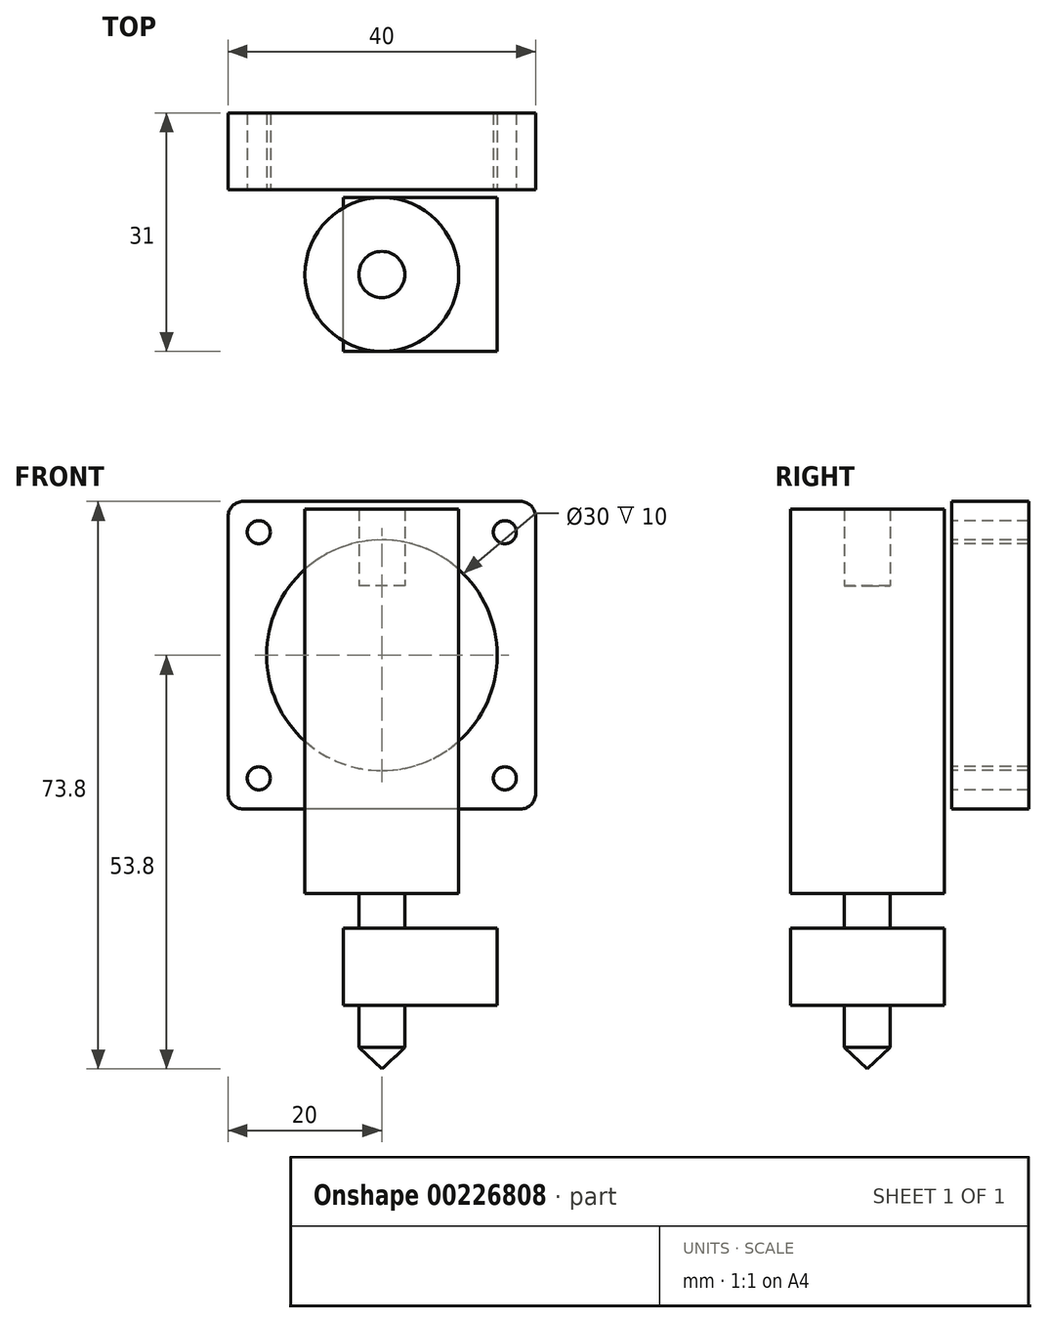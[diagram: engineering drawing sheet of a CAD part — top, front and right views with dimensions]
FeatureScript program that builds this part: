
annotation { "Feature Type Name" : "Feature", "Feature Type Description" : "" }
export const myFeature = defineFeature(function(context is Context, id is Id, definition is map)
    precondition{}
    {
        {
            var Q0;
            Q0=qCreatedBy(makeId("Top.planeOp"),FACE);
            var sketch = newSketch(context, id + "F0", { "sketchPlane" : qUnion([Q0])});
            skCircle(sketch, "E0", {"center": v(0, 0) * mm, "radius": 8 * mm});
            skCircle(sketch, "E1", {"center": v(0, 0) * mm, "radius": 10 * mm});
            skCircle(sketch, "E2", {"center": v(0, 0) * mm, "radius": 3 * mm});
            skSolve(sketch);
        }
        {
            var Q0;
            Q0=makeQuery(id+"F0.imprint","IMPRINT",FACE,{"disambiguationData":[TD([[makeQuery(id+"F0.imprint","IMPRINT",EDGE,{"derivedFrom":sQuery(id+"F0.wireOp",EDGE,"E0")}),1.0]])]});
            var Q1;
            Q1=makeQuery(id+"F0.imprint","IMPRINT",FACE,{"disambiguationData":[TD([[makeQuery(id+"F0.imprint","IMPRINT",EDGE,{"derivedFrom":sQuery(id+"F0.wireOp",EDGE,"E0")}),-1.0]])]});
            extrude(context, id + "F1", {"entities" : qUnion([Q0, Q1]), "depth" : 10 * mm});
        }
        {
            var Q0;
            Q0=makeQuery(id+"F0.imprint","IMPRINT",FACE,{"disambiguationData":[TD([[makeQuery(id+"F0.imprint","IMPRINT",EDGE,{"derivedFrom":sQuery(id+"F0.wireOp",EDGE,"E0")}),-1.0]])]});
            var Q1;
            Q1=makeQuery(id+"F0.imprint","IMPRINT",FACE,{"disambiguationData":[TD([[makeQuery(id+"F0.imprint","IMPRINT",EDGE,{"derivedFrom":sQuery(id+"F0.wireOp",EDGE,"E0")}),1.0]])]});
            var Q2;
            Q2=makeQuery(id+"F0.imprint","IMPRINT",FACE,{"disambiguationData":[TD([[makeQuery(id+"F0.imprint","IMPRINT",EDGE,{"derivedFrom":sQuery(id+"F0.wireOp",EDGE,"E2")}),1.0]])]});
            extrude(context, id + "F2", {"entities" : qUnion([Q0, Q1, Q2]), "operationType" : NewBodyOperationType.ADD, "oppositeDirection" : true, "depth" : 40 * mm});
        }
        {
            var Q0;
            Q0=makeQuery(id+"F0.imprint","IMPRINT",FACE,{"disambiguationData":[TD([[makeQuery(id+"F0.imprint","IMPRINT",EDGE,{"derivedFrom":sQuery(id+"F0.wireOp",EDGE,"E2")}),1.0]])]});
            extrude(context, id + "F3", {"entities" : qUnion([Q0]), "operationType" : NewBodyOperationType.ADD, "oppositeDirection" : true, "depth" : 60 * mm});
        }
        {
            var Q0;
            Q0=qCreatedBy(makeId("Front.planeOp"),FACE);
            var sketch = newSketch(context, id + "F4", { "sketchPlane" : qUnion([Q0])});
            skLineSegment(sketch, "E3.0", {"start": v(-3, -44.5) * mm, "end": v(3, -44.5) * mm});
            skLineSegment(sketch, "E4", {"start": v(0, 0) * mm, "end": v(0, -62.8) * mm, "construction": true});
            skPoint(sketch, "E4.endSnap0", {"position": v(0, -44.5) * mm});
            skLineSegment(sketch, "E5.bottom", {"start": v(-5, -44.5) * mm, "end": v(15, -44.5) * mm});
            skLineSegment(sketch, "E5.top", {"start": v(-5, -54.5) * mm, "end": v(15, -54.5) * mm});
            skLineSegment(sketch, "E5.left", {"start": v(-5, -44.5) * mm, "end": v(-5, -54.5) * mm});
            skLineSegment(sketch, "E5.right", {"start": v(15, -44.5) * mm, "end": v(15, -54.5) * mm});
            skPoint(sketch, "E6", {"position": v(0, -62.8) * mm});
            skSolve(sketch);
        }
        {
            var Q0;
            Q0=qSketchRegion(id+"F4",true);
            extrude(context, id + "F5", {"entities" : qUnion([Q0]), "operationType" : NewBodyOperationType.ADD, "endBound" : BoundingType.SYMMETRIC, "depth" : 20 * mm});
        }
        {
            var Q1;
            Q1=makeQuery(id+"F3.opExtrude","CAP_FACE",FACE,{"disambiguationData":[OSD([sQuery(id+"F0.wireOp",EDGE,"E2")])],"isStart":false});
            var Q2;
            Q2=sQuery(id+"F4.wireOp",VERTEX,"E6");
            loft(context, id + "F6", {"operationType" : NewBodyOperationType.ADD, "sheetProfilesArray" : [{ "sheetProfileEntities" : qUnion([Q1]) }, { "sheetProfileEntities" : qUnion([Q2]) }]});
        }
        {
            var Q0;
            Q0=qCreatedBy(makeId("Front.planeOp"),FACE);
            var sketch = newSketch(context, id + "F7", { "sketchPlane" : qUnion([Q0])});
            skLineSegment(sketch, "E7.bottom", {"start": v(20, 20) * mm, "end": v(-20, 20) * mm});
            skLineSegment(sketch, "E7.top", {"start": v(20, -20) * mm, "end": v(-20, -20) * mm});
            skLineSegment(sketch, "E7.left", {"start": v(20, 20) * mm, "end": v(20, -20) * mm});
            skLineSegment(sketch, "E7.right", {"start": v(-20, 20) * mm, "end": v(-20, -20) * mm});
            skPoint(sketch, "E7.middle", {"position": v(0, 0) * mm});
            skCircle(sketch, "E8", {"center": v(0, 0) * mm, "radius": 15 * mm});
            skLineSegment(sketch, "E9.bottom", {"start": v(16, 16) * mm, "end": v(-16, 16) * mm, "construction": true});
            skLineSegment(sketch, "E9.top", {"start": v(16, -16) * mm, "end": v(-16, -16) * mm, "construction": true});
            skLineSegment(sketch, "E9.left", {"start": v(16, 16) * mm, "end": v(16, -16) * mm, "construction": true});
            skLineSegment(sketch, "E9.right", {"start": v(-16, 16) * mm, "end": v(-16, -16) * mm, "construction": true});
            skCircle(sketch, "E10", {"center": v(-16, 16) * mm, "radius": 1.5 * mm});
            skCircle(sketch, "E11", {"center": v(16, 16) * mm, "radius": 1.5 * mm});
            skCircle(sketch, "E12", {"center": v(16, -16) * mm, "radius": 1.5 * mm});
            skCircle(sketch, "E13", {"center": v(-16, -16) * mm, "radius": 1.5 * mm});
            skSolve(sketch);
        }
        {
            var Q0;
            Q0=makeQuery(id+"F7.imprint","IMPRINT",FACE,{"disambiguationData":[TD([[makeQuery(id+"F7.imprint","IMPRINT",EDGE,{"derivedFrom":sQuery(id+"F7.wireOp",EDGE,"E7.bottom")}),1.0]])]});
            extrude(context, id + "F8", {"entities" : qUnion([Q0]), "oppositeDirection" : true, "depth" : 10 * mm});
        }
        {
            var Q0;
            Q0=makeQuery(id+"F8.opExtrude","SWEPT_EDGE",EDGE,{"disambiguationData":[OSD([sQuery(id+"F7.wireOp",EDGE,"E7.bottom"),sQuery(id+"F7.wireOp",EDGE,"E7.right")])]});
            var Q1;
            Q1=makeQuery(id+"F8.opExtrude","SWEPT_EDGE",EDGE,{"disambiguationData":[OSD([sQuery(id+"F7.wireOp",EDGE,"E7.bottom"),sQuery(id+"F7.wireOp",EDGE,"E7.left")])]});
            var Q2;
            Q2=makeQuery(id+"F8.opExtrude","SWEPT_EDGE",EDGE,{"disambiguationData":[OSD([sQuery(id+"F7.wireOp",EDGE,"E7.top"),sQuery(id+"F7.wireOp",EDGE,"E7.left")])]});
            var Q3;
            Q3=makeQuery(id+"F8.opExtrude","SWEPT_EDGE",EDGE,{"disambiguationData":[OSD([sQuery(id+"F7.wireOp",EDGE,"E7.top"),sQuery(id+"F7.wireOp",EDGE,"E7.right")])]});
            fillet(context, id + "F9", {"entities" : qUnion([Q0, Q1, Q2, Q3]), "radius" : 2 * mm, "tangentPropagation" : true, "allowEdgeOverflow" : false});
        }
        {
            var Q0;
            Q0=makeQuery(id+"F8.opExtrude","SWEPT_BODY",BODY,{"disambiguationData":[OSD([sQuery(id+"F7.wireOp",EDGE,"E7.bottom"),sQuery(id+"F7.wireOp",EDGE,"E7.top"),sQuery(id+"F7.wireOp",EDGE,"E7.left"),sQuery(id+"F7.wireOp",EDGE,"E7.right"),sQuery(id+"F7.wireOp",EDGE,"E8"),sQuery(id+"F7.wireOp",EDGE,"E10"),sQuery(id+"F7.wireOp",EDGE,"E11"),sQuery(id+"F7.wireOp",EDGE,"E12"),sQuery(id+"F7.wireOp",EDGE,"E13")])]});
            transform(context, id + "F10", {"entities" : qUnion([Q0]), "transformType" : TransformType.TRANSLATION_3D, "dx" : 0 * mm, "dy" : 11 * mm, "dz" : -9 * mm, "makeCopy" : false});
        }
    });
